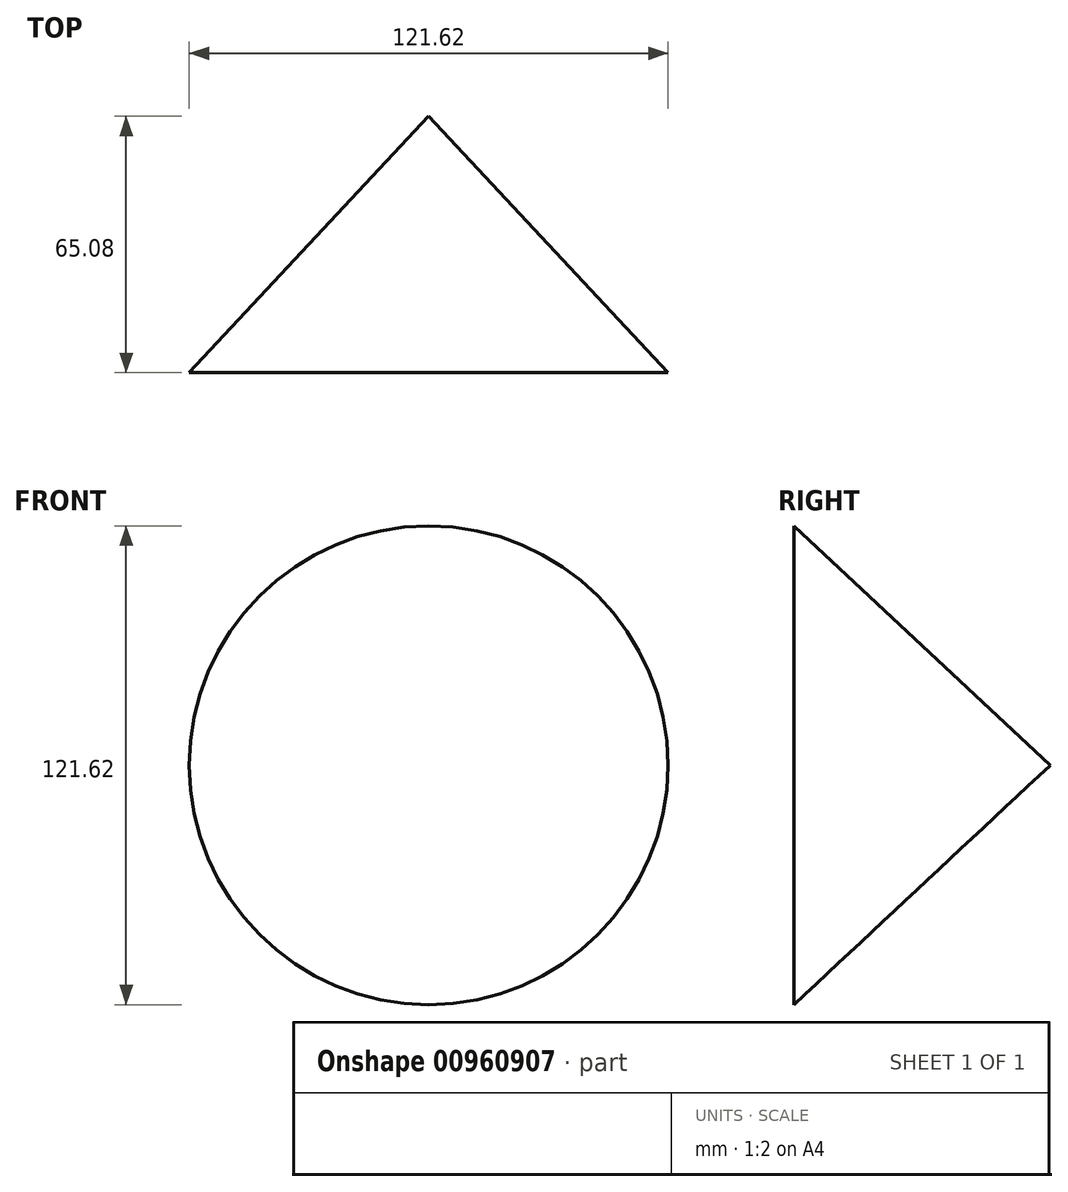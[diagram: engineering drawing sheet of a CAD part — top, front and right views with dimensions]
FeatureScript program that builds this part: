
annotation { "Feature Type Name" : "Feature", "Feature Type Description" : "" }
export const myFeature = defineFeature(function(context is Context, id is Id, definition is map)
    precondition{}
    {
        {
            var Q0;
            Q0=qCreatedBy(makeId("Top.planeOp"),FACE);
            var sketch = newSketch(context, id + "F0", { "sketchPlane" : qUnion([Q0])});
            skLineSegment(sketch, "E0", {"start": v(0, 0) * mm, "end": v(-60.8, 0) * mm});
            skLineSegment(sketch, "E1", {"start": v(-60.8, 0) * mm, "end": v(0, 65.08) * mm});
            skLineSegment(sketch, "E2", {"start": v(0, 65.08) * mm, "end": v(0, 0) * mm});
            skSolve(sketch);
        }
        {
            var Q0;
            Q0=makeQuery(id+"F0.imprint","IMPRINT",FACE,{"disambiguationData":[TD([[makeQuery(id+"F0.imprint","IMPRINT",EDGE,{"derivedFrom":sQuery(id+"F0.wireOp",EDGE,"E0")}),-1.0]])]});
            var Q1;
            Q1=sQuery(id+"F0.wireOp",EDGE,"E2");
            revolve(context, id + "F1", {"surfaceOperationType" : NewSurfaceOperationType.NEW, "entities" : qUnion([Q0]), "axis" : qUnion([Q1]), "revolveType" : RevolveType.FULL});
        }
    });
